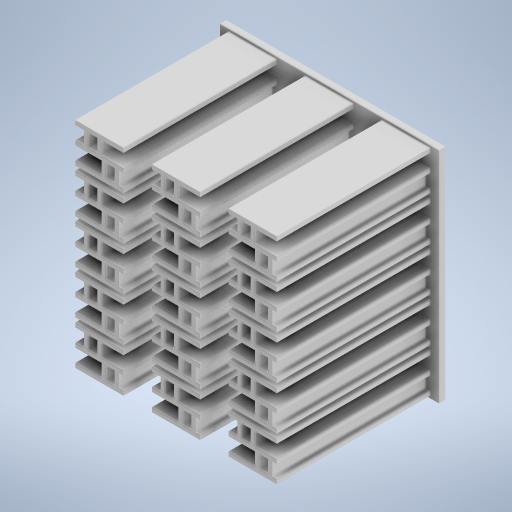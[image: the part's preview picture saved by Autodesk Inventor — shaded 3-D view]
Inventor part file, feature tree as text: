
AUTODESK INVENTOR PART (.ipt)
format: ipt  version: 2023 (Build 270158000, 158)  size: 758,784 bytes
history: native  units: mm
features: projected_geometry x4, extrude x2, sketch x2, pattern_linear x1
ambient origin geometry x8: Origin, YZ Plane, XZ Plane, XY Plane, X Axis, Y Axis, Z Axis, Center Point
bodies: Solid1 (feature_tree)
feature tree (9):
  extrude  "Extrusion1"  Depth=22.0mm
  pattern_linear  "Rectangular Pattern1"  Spacing1=2.0mm  [1 undecoded]
  extrude  "Extrusion3"  Depth=4.0mm
  sketch  "Sketch1"  dims[d0=2.0mm d1=22.0mm]
  sketch  "Sketch4"  dims[d2=2.0mm d3=2.0mm d4=4.0mm d5=4.0mm d7=2.0mm d8=2.0mm d9=2.0mm d10=2.0mm d13=4.0mm d14=2.0mm d15=2.0mm d16=2.0mm d17=2.0mm d18=2.0mm d20=2.0mm d21=2.0mm d22=2.0mm d23=6.0mm d24=6.0mm d25=6.0mm d26=2.0mm d27=6.0mm d28=6.0mm d29=1.0mm d30=2.0mm d31=2.0mm d32=1.0mm d33=70.0mm d34=0.0mm d41=30.0mm d43=35.0mm d44=50.0mm d46=20.0mm d47=1.0mm d48=1.0mm d49=4.0mm d50=4.0mm d51=3.0mm d52=0.0mm d53=13.0mm d54=13.0mm d55=2.0mm]
  projected_geometry  "Projected Loop2"
  projected_geometry  "Projected Loop3"
  projected_geometry  "Projected Loop4"
  projected_geometry  "Projected Loop5"
note: 1 required parameter value undecoded (feature->parameter linkage not recoverable at this tier; creation-order binding heuristic only, values carry confidence <= 0.55)
